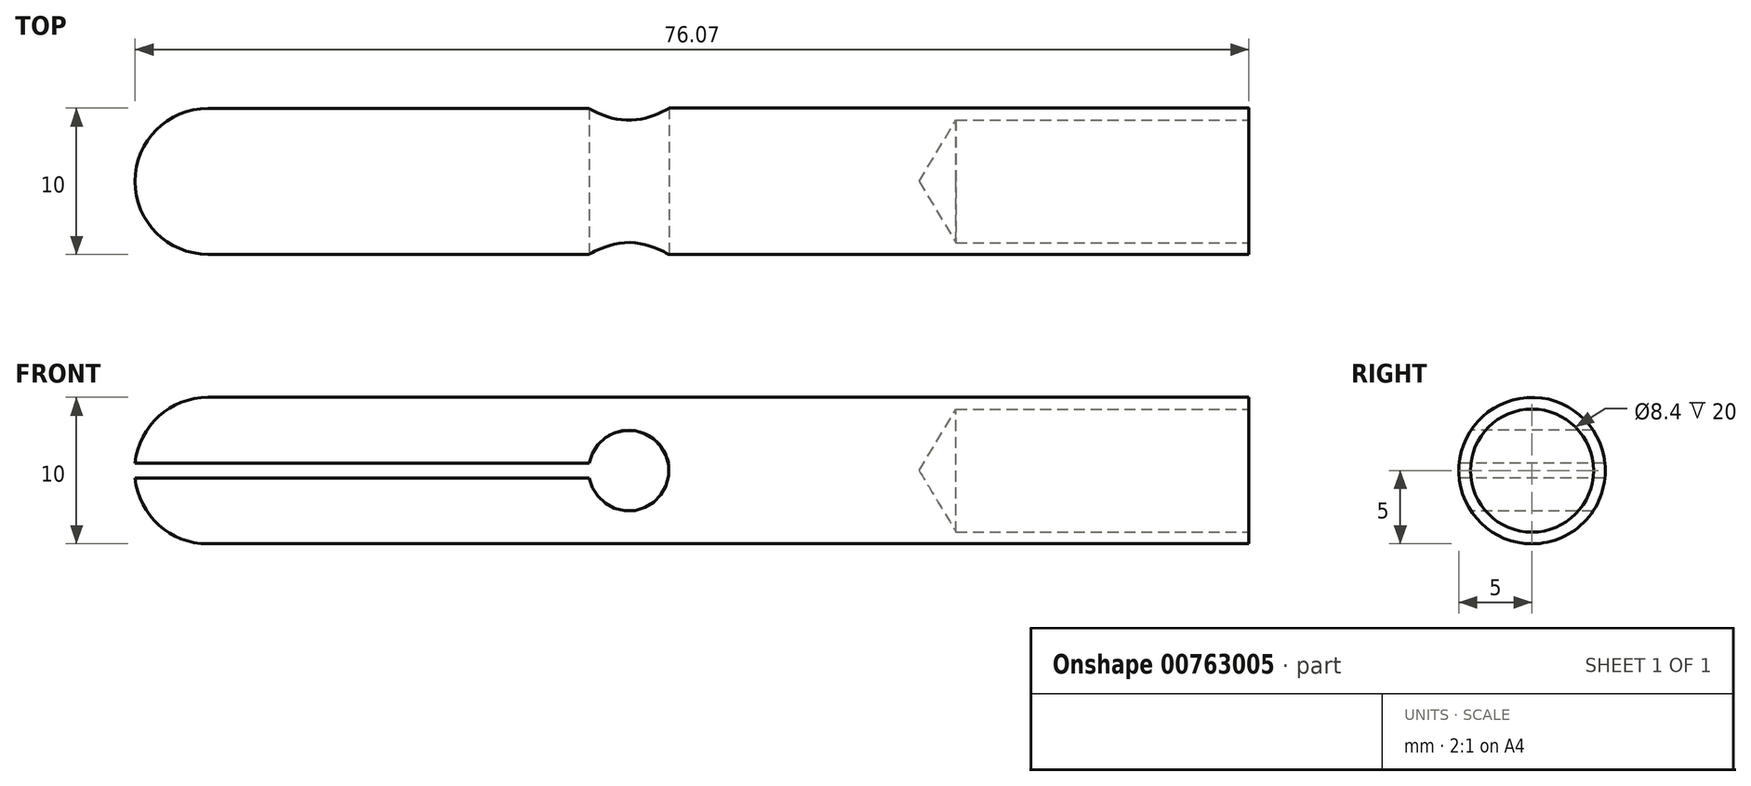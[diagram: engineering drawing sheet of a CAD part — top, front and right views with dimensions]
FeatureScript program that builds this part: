
annotation { "Feature Type Name" : "Feature", "Feature Type Description" : "" }
export const myFeature = defineFeature(function(context is Context, id is Id, definition is map)
    precondition{}
    {
        {
            var Q0;
            Q0=qCreatedBy(makeId("Right.planeOp"),FACE);
            var sketch = newSketch(context, id + "F0", { "sketchPlane" : qUnion([Q0])});
            skCircle(sketch, "E0", {"center": v(0, 0) * mm, "radius": 5 * mm});
            skSolve(sketch);
        }
        {
            var Q0;
            Q0=makeQuery(id+"F0.imprint","IMPRINT",FACE,{"disambiguationData":[TD([[makeQuery(id+"F0.imprint","IMPRINT",EDGE,{"derivedFrom":sQuery(id+"F0.wireOp",EDGE,"E0")}),1.0]])]});
            extrude(context, id + "F1", {"entities" : qUnion([Q0]), "depth" : 76.1 * mm, "offsetDistance" : 25 * mm});
        }
        {
            var Q0;
            Q0=makeQuery(id+"F1.opExtrude","CAP_EDGE",EDGE,{"disambiguationData":[OSD([sQuery(id+"F0.wireOp",EDGE,"E0")])],"isStart":true});
            fillet(context, id + "F2", {"entities" : qUnion([Q0]), "radius" : 5 * mm, "tangentPropagation" : true, "allowEdgeOverflow" : false});
        }
        {
            var Q0;
            Q0=qCreatedBy(makeId("Right.planeOp"),FACE);
            var sketch = newSketch(context, id + "F3", { "sketchPlane" : qUnion([Q0])});
            skLineSegment(sketch, "E1.bottom", {"start": v(-5, 0.5) * mm, "end": v(5, 0.5) * mm});
            skLineSegment(sketch, "E1.top", {"start": v(-5, -0.5) * mm, "end": v(5, -0.5) * mm});
            skLineSegment(sketch, "E1.left", {"start": v(-5, 0.5) * mm, "end": v(-5, -0.5) * mm});
            skLineSegment(sketch, "E1.right", {"start": v(5, 0.5) * mm, "end": v(5, -0.5) * mm});
            skPoint(sketch, "E1.middle", {"position": v(0, 0) * mm});
            skSolve(sketch);
        }
        {
            var Q0;
            Q0=makeQuery(id+"F3.imprint","IMPRINT",FACE,{"disambiguationData":[TD([[makeQuery(id+"F3.imprint","IMPRINT",EDGE,{"derivedFrom":sQuery(id+"F3.wireOp",EDGE,"E1.bottom")}),-1.0]])]});
            extrude(context, id + "F4", {"entities" : qUnion([Q0]), "operationType" : NewBodyOperationType.REMOVE, "depth" : (36.5 - 2.75) * mm, "offsetDistance" : 25 * mm});
        }
        {
            var Q0;
            Q0=qCreatedBy(makeId("Front.planeOp"),FACE);
            var sketch = newSketch(context, id + "F5", { "sketchPlane" : qUnion([Q0])});
            skCircle(sketch, "E2", {"center": v(33.75, 0) * mm, "radius": 2.75 * mm});
            skSolve(sketch);
        }
        {
            var Q0;
            Q0 = qSketchRegion(id + "F5", true);
            extrude(context, id + "F6", {"entities" : qUnion([Q0]), "operationType" : NewBodyOperationType.REMOVE, "endBound" : BoundingType.SYMMETRIC, "oppositeDirection" : true, "depth" : 25 * mm, "offsetDistance" : 25 * mm});
        }
        {
            var Q0;
            Q0=makeQuery(id+"F1.opExtrude","CAP_FACE",FACE,{"disambiguationData":[OSD([sQuery(id+"F0.wireOp",EDGE,"E0")])],"isStart":false});
            var sketch = newSketch(context, id + "F7", { "sketchPlane" : qUnion([Q0])});
            skPoint(sketch, "E3", {"position": v(0, 0) * mm});
            skSolve(sketch);
        }
        {
            var Q0;
            Q0=sQuery(id+"F7.wireOp",VERTEX,"E3");
            var Q1;
            Q1=makeQuery(id+"F1.opExtrude","SWEPT_BODY",BODY,{"disambiguationData":[OSD([sQuery(id+"F0.wireOp",EDGE,"E0")])]});
            hole(context, id + "F8", {"style" : HoleStyle.SIMPLE, "endStyle" : HoleEndStyle.BLIND, "standardTappedOrClearance" : lookupTablePath({ "standard" : "ISO", "fit" : "Close", "size" : "M8", "type" : "Clearance" }), "standardBlindInLast" : lookupTablePath({ "fit" : "Close", "standard" : "ISO", "size" : "M8", "type" : "Clearance" }), "holeDiameter" : 8.4 * mm, "majorDiameter" : 5 * mm, "holeDepth" : 20 * mm, "isTappedThrough" : true, "tappedDepth" : 12 * mm, "tapClearance" : 3, "startFromSketch" : true, "locations" : qUnion([Q0]), "scope" : qUnion([Q1])});
        }
    });
